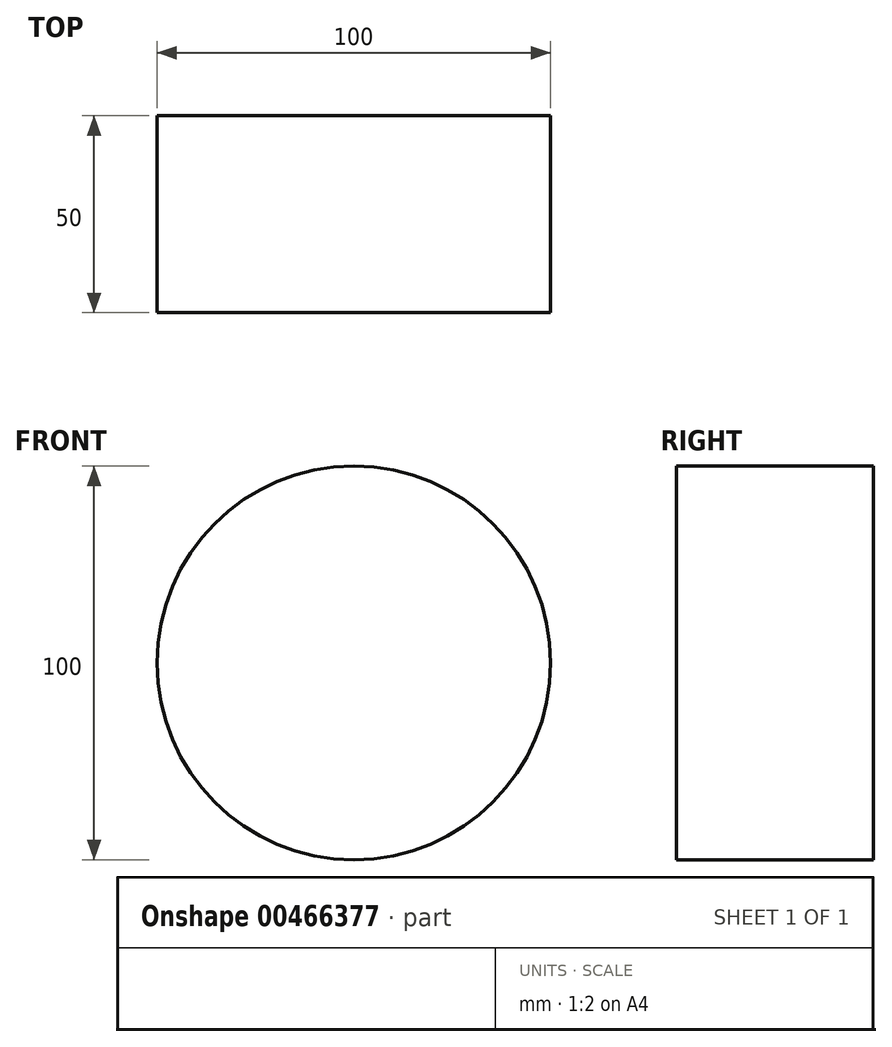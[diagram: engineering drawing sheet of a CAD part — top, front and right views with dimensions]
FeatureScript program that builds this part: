
annotation { "Feature Type Name" : "Feature", "Feature Type Description" : "" }
export const myFeature = defineFeature(function(context is Context, id is Id, definition is map)
    precondition{}
    {
        {
            var Q0;
            Q0=qCreatedBy(makeId("Front.planeOp"),FACE);
            var sketch = newSketch(context, id + "F0", { "sketchPlane" : qUnion([Q0])});
            skCircle(sketch, "E0", {"center": v(0, 0) * mm, "radius": 50 * mm});
            skSolve(sketch);
        }
        {
            var Q0;
            Q0=makeQuery(id+"F0.imprint","IMPRINT",FACE,{"disambiguationData":[TD([[makeQuery(id+"F0.imprint","IMPRINT",EDGE,{"derivedFrom":sQuery(id+"F0.wireOp",EDGE,"E0")}),1.0]])]});
            var Q1;
            Q1=sQuery(id+"F0.wireOp",EDGE,"E0");
            extrude(context, id + "F1", {"entities" : qUnion([Q0]), "surfaceEntities" : qUnion([Q1]), "depth" : 50 * mm});
        }
    });
